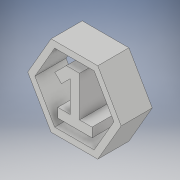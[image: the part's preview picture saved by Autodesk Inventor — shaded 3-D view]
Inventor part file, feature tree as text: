
AUTODESK INVENTOR PART (.ipt)
format: ipt  version: 2019 (Build 230136000, 136)  size: 129,536 bytes
history: native  units: mm
features: extrude x1, sketch x1
ambient origin geometry x8: Origin, YZ Plane, XZ Plane, XY Plane, X Axis, Y Axis, Z Axis, Center Point
bodies: Solid1 (feature_tree)
feature tree (2):
  extrude  "Extrusion1"  Depth=1.0mm
  sketch  "Sketch1"  dims[d0=15.0mm d1=1.0mm d2=1.5mm d3=1.5mm d4=1.5mm d5=1.5mm d6=2.0mm d7=2.0mm d8=2.0mm d9=1.5mm d10=1.5mm d11=0.5mm d12=45.0deg d13=5.0mm d14=0.0mm]
